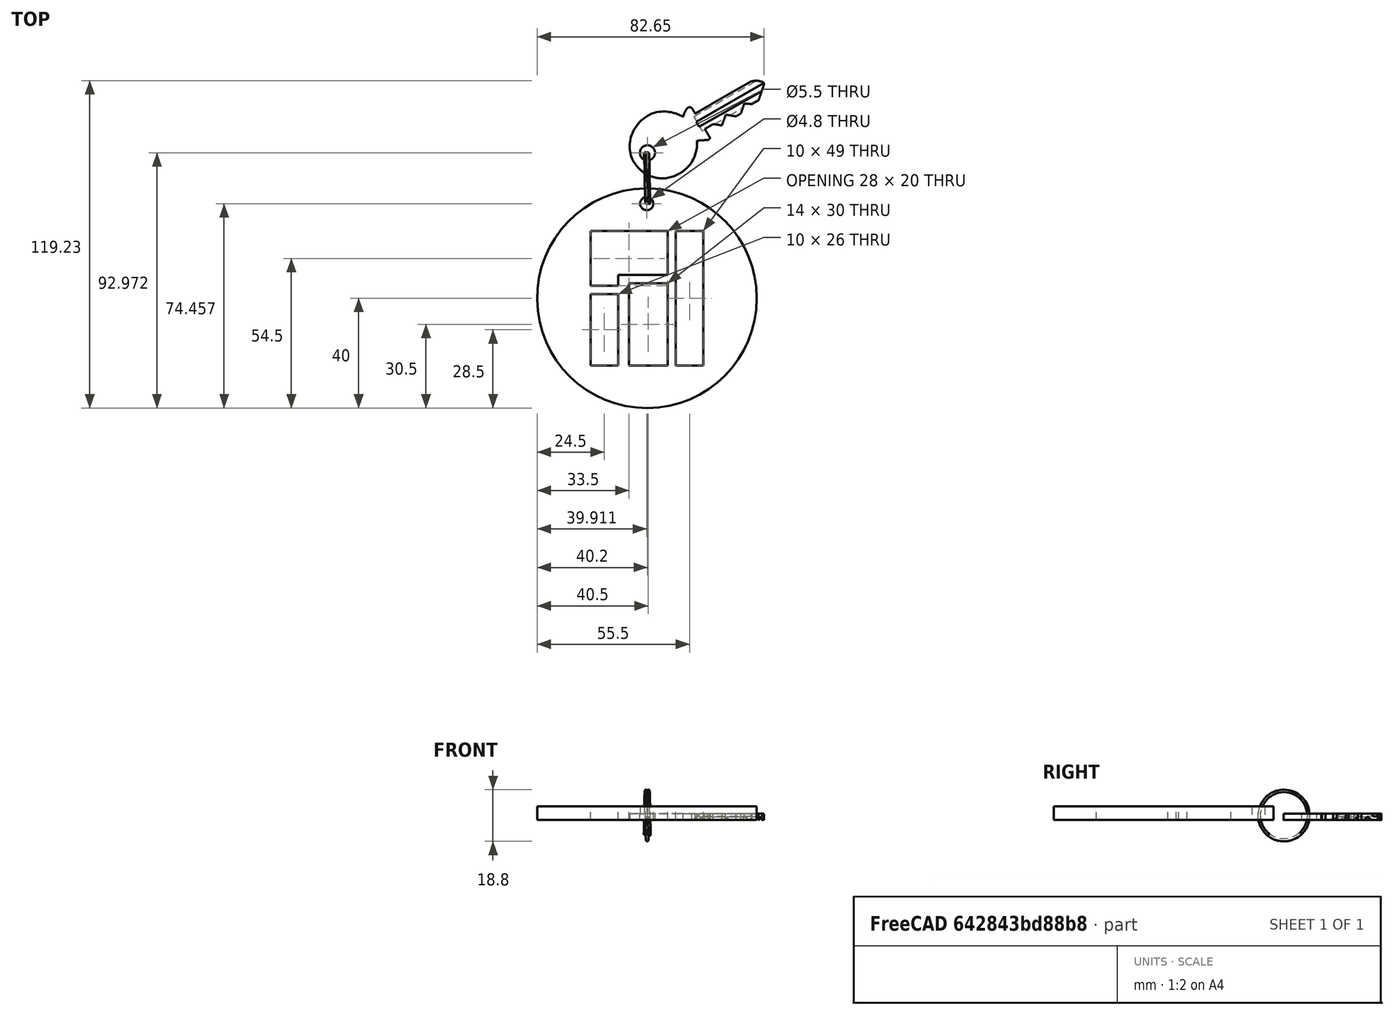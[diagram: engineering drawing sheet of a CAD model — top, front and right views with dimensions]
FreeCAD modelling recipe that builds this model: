
FCSTD DOCUMENT  (FreeCAD 0.17R13509 (Git))
Label: Manjaro2
License: CreativeCommons Attribution-ShareAlike
LicenseURL: http://creativecommons.org/licenses/by-sa/4.0/
objects: Part::Feature×2, Sketcher::SketchObject×1, PartDesign::Pad×1, App::DocumentObjectGroup×1
note: 5 computed .brp shape members not serialized (recipe doc carries the construction recipe); baked Part::Feature solids carry a one-line shape summary decoded from their .brp

FEATURE [Part::Feature] Sweep  label="key-ring-model-1"
  Placement = pos=(-1.2,30.2546,1.6391) rot=(0.333333,0.881918,0.333333;1.69612rad)
  shape: bbox 3.31 x 27.02 x 26.33 mm, 4 faces (baked)
FEATURE [Part::Feature] Cut  label="key-model-1"
  Placement = pos=(-5.46976,36.5266,0) rot=(0,0,1;0.517888rad)
  shape: bbox 49.82 x 36.6 x 2.3 mm, 44 faces (baked)
FEATURE [Sketcher::SketchObject] Sketch
  MapMode = 5
  Placement = pos=(-21,-38,0) rot=(0,0,1;0rad)
  sketch-geometry (27):
    g0: LineSegment StartX=0 StartY=0 StartZ=0 EndX=0 EndY=26 EndZ=0
    g1: LineSegment StartX=0 StartY=26 StartZ=0 EndX=10 EndY=26 EndZ=0
    g2: LineSegment StartX=10 StartY=26 StartZ=0 EndX=10 EndY=0 EndZ=0
    g3: LineSegment StartX=10 StartY=0 StartZ=0 EndX=0 EndY=0 EndZ=0
    g4: LineSegment StartX=0 StartY=29 StartZ=0 EndX=0 EndY=49 EndZ=0
    g5: LineSegment StartX=0 StartY=49 StartZ=0 EndX=28 EndY=49 EndZ=0
    g6: LineSegment StartX=28 StartY=49 StartZ=0 EndX=28 EndY=33 EndZ=0
    g7: LineSegment StartX=28 StartY=33 StartZ=0 EndX=10 EndY=33 EndZ=0
    g8: LineSegment StartX=10 StartY=33 StartZ=0 EndX=10 EndY=29 EndZ=0
    g9: LineSegment StartX=10 StartY=29 StartZ=0 EndX=0 EndY=29 EndZ=0
    g10: LineSegment StartX=14 StartY=30 StartZ=0 EndX=28 EndY=30 EndZ=0
    g11: LineSegment StartX=28 StartY=30 StartZ=0 EndX=28 EndY=0 EndZ=0
    g12: LineSegment StartX=28 StartY=0 StartZ=0 EndX=14 EndY=0 EndZ=0
    g13: LineSegment StartX=14 StartY=0 StartZ=0 EndX=14 EndY=30 EndZ=0
    g14: LineSegment StartX=31 StartY=49 StartZ=0 EndX=41 EndY=49 EndZ=0
    g15: LineSegment StartX=41 StartY=49 StartZ=0 EndX=41 EndY=0 EndZ=0
    g16: LineSegment StartX=41 StartY=0 StartZ=0 EndX=31 EndY=0 EndZ=0
    g17: LineSegment StartX=31 StartY=0 StartZ=0 EndX=31 EndY=49 EndZ=0
    g18: LineSegment [constr] StartX=28 StartY=49 StartZ=0 EndX=31 EndY=49 EndZ=0
    g19: LineSegment [constr] StartX=28 StartY=33 StartZ=0 EndX=28 EndY=30 EndZ=0
    g20: LineSegment [constr] StartX=20.5 StartY=49 StartZ=0 EndX=20.5 EndY=24.5 EndZ=0
    g21: LineSegment [constr] StartX=20.5 StartY=24.5 StartZ=0 EndX=20.5 EndY=0 EndZ=0
    g22: LineSegment [constr] StartX=0 StartY=24.5 StartZ=0 EndX=20.5 EndY=24.5 EndZ=0
    g23: LineSegment [constr] StartX=20.5 StartY=24.5 StartZ=0 EndX=41 EndY=24.5 EndZ=0
    g24: Circle CenterX=20.5 CenterY=24.5 CenterZ=0 NormalX=0 NormalY=0 NormalZ=1 AngleXU=0 Radius=40
    g25: Circle CenterX=20.411 CenterY=58.9566 CenterZ=0 NormalX=0 NormalY=0 NormalZ=1 AngleXU=0 Radius=2.39787
    g26: LineSegment [constr] StartX=20.5 StartY=48.9566 StartZ=0 EndX=20.411 EndY=58.9566 EndZ=0
  constraints (75):
    c: Coincident(g0,g1)
    c: Vertical(g0)
    c: Horizontal(g1)
    c: Vertical(g2)
    c: Coincident(g3,g0)
    c: DistanceY(g0,g0) = 26
    c: Coincident(g4,g9)
    c: Horizontal(g9)
    c: DistanceY(g0,g4) = 3
    c: DistanceY(g4,g4) = 20
    c: Coincident(g5,g6)
    c: Vertical(g6)
    c: Coincident(g6,g7)
    c: Horizontal(g7)
    c: DistanceX(g5,g5) = 28
    c: Horizontal(g5)
    c: Coincident(g7,g8)
    c: Vertical(g8)
    c: Coincident(g9,g8)
    c: Vertical(g4)
    c: PointOnObject(g4,g-2)
    c: PointOnObject(g0,g-2)
    c: PointOnObject(g0,g-1)
    c: Coincident(g4,g5)
    c: Coincident(g10,g11)
    c: Coincident(g11,g12)
    c: Coincident(g12,g13)
    c: Coincident(g13,g10)
    c: Horizontal(g10)
    c: Horizontal(g12)
    c: Vertical(g11)
    c: Vertical(g13)
    c: Horizontal(g3)
    c: Coincident(g1,g2)
    c: Equal(g1,g9)
    c: PointOnObject(g12,g-1)
    c: DistanceX(g3,g12) = 4
    c: Coincident(g14,g15)
    c: Coincident(g15,g16)
    c: Coincident(g16,g17)
    c: Coincident(g17,g14)
    c: Horizontal(g14)
    c: Horizontal(g16)
    c: Vertical(g17)
    c: PointOnObject(g15,g-1)
    c: DistanceX(g14,g14) = 10
    c: Horizontal(g18)
    c: Coincident(g18,g14)
    c: Coincident(g18,g5)
    c: DistanceX(g18,g18) = 3
    c: DistanceY(g13,g13) = 30
    c: Vertical(g19)
    c: Coincident(g10,g19)
    c: Coincident(g6,g19)
    c: Coincident(g2,g3)
    c: Vertical(g15)
    c: DistanceX(g9,g9) = 10
    c: Coincident(g20,g21)
    c: PointOnObject(g20,g5)
    c: Vertical(g20)
    c: Equal(g20,g21)
    c: Vertical(g21)
    c: Coincident(g22,g23)
    c: Equal(g23,g22)
    c: Coincident(g20,g22)
    c: PointOnObject(g23,g15)
    c: PointOnObject(g22,g0)
    c: Horizontal(g23)
    c: Horizontal(g22)
    c: PointOnObject(g21,g12)
    c: Radius(g24) = 40
    c: DistanceY(g19,g19) = 3
    c: Coincident(g24,g20)
    c: Coincident(g25,g26)
    c: DistanceY(g26,g26) = 10
FEATURE [PartDesign::Pad] Pad
  Length = 5
  Length2 = 100
  Placement = pos=(-21,-38,0) rot=(0,0,1;0rad)
  Profile = -> Sketch
  Refine = true
  Type = 0
FEATURE [App::DocumentObjectGroup] Group  label="Assembly"
  Group = -> [Sweep,Cut,Pad]
